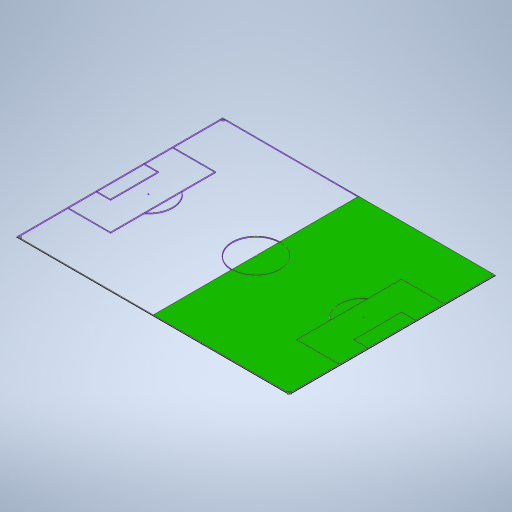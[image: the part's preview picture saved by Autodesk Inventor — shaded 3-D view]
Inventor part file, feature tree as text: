
AUTODESK INVENTOR PART (.ipt)
format: ipt  version: 2024.1 (Build 281209000, 209)  size: 520,704 bytes
history: native  units: in
note: dims shown in document units (in); Inventor stores cm internally (conversion verified against a paired STEP export)
features: extrude x42, sketch x1
ambient origin geometry x8: Origin, YZ Plane, XZ Plane, XY Plane, X Axis, Y Axis, Z Axis, Center Point
bodies: Solid3 (feature_tree), Solid4 (feature_tree), Solid5 (feature_tree), Solid6 (feature_tree), Solid7 (feature_tree), Solid8 (feature_tree), Solid9 (feature_tree), Solid10 (feature_tree), Solid11 (feature_tree)
feature tree (43):
  sketch  "Sketch2"  dims[d126=10.0in d127=0.0in d128=10.0in d129=0.0in d130=10.0in d131=0.0in d132=10.0in d133=0.0in d134=10.0in d135=0.0in d136=10.0in d137=0.0in d138=10.0in d139=0.0in d140=10.0in d141=0.0in d142=10.0in d143=0.0in d144=10.0in d145=0.0in d146=10.0in d147=0.0in d148=10.0in d149=0.0in d150=10.0in d151=0.0in d152=10.0in d153=0.0in d154=10.0in d155=0.0in d156=10.0in d157=0.0in d158=10.0in d159=0.0in d160=10.0in d161=0.0in d162=10.0in d163=0.0in d164=10.0in d165=0.0in d166=10.0in d167=0.0in d168=10.0in d169=0.0in d170=10.0in d171=0.0in d172=10.0in d173=0.0in d174=10.0in d175=0.0in d176=10.0in d177=0.0in d178=10.0in d179=0.0in d180=10.0in d181=0.0in d182=10.0in d183=0.0in d184=10.0in d185=0.0in d186=10.0in d187=0.0in d188=10.0in d189=0.0in d190=10.0in d191=0.0in d192=10.0in d193=0.0in d194=10.0in d195=0.0in d196=10.0in d197=0.0in d198=10.0in d199=0.0in d200=10.0in d201=0.0in d202=10.0in d203=0.0in d204=10.0in d205=0.0in d206=10.0in d207=0.0in d208=10.0in d209=0.0in]
  extrude  "Extrusion26"  Depth=10.0in TaperAngle=0.0deg
  extrude  "Extrusion27"  Depth=10.0in TaperAngle=0.0deg
  extrude  "Extrusion28"  Depth=10.0in TaperAngle=0.0deg
  extrude  "Extrusion29"  Depth=10.0in TaperAngle=0.0deg
  extrude  "Extrusion30"  Depth=10.0in TaperAngle=0.0deg
  extrude  "Extrusion31"  Depth=10.0in TaperAngle=0.0deg
  extrude  "Extrusion32"  Depth=10.0in TaperAngle=0.0deg
  extrude  "Extrusion33"  Depth=10.0in TaperAngle=0.0deg
  extrude  "Extrusion34"  Depth=10.0in TaperAngle=0.0deg
  extrude  "Extrusion35"  Depth=10.0in TaperAngle=0.0deg
  extrude  "Extrusion36"  Depth=10.0in TaperAngle=0.0deg
  extrude  "Extrusion37"  Depth=10.0in TaperAngle=0.0deg
  extrude  "Extrusion38"  Depth=10.0in TaperAngle=0.0deg
  extrude  "Extrusion39"  Depth=10.0in TaperAngle=0.0deg
  extrude  "Extrusion40"  Depth=10.0in TaperAngle=0.0deg
  extrude  "Extrusion41"  Depth=10.0in TaperAngle=0.0deg
  extrude  "Extrusion42"  Depth=10.0in TaperAngle=0.0deg
  extrude  "Extrusion43"  Depth=10.0in TaperAngle=0.0deg
  extrude  "Extrusion44"  Depth=10.0in TaperAngle=0.0deg
  extrude  "Extrusion45"  Depth=10.0in TaperAngle=0.0deg
  extrude  "Extrusion46"  Depth=10.0in TaperAngle=0.0deg
  extrude  "Extrusion47"  Depth=10.0in TaperAngle=0.0deg
  extrude  "Extrusion48"  Depth=10.0in TaperAngle=0.0deg
  extrude  "Extrusion49"  Depth=10.0in TaperAngle=0.0deg
  extrude  "Extrusion50"  Depth=10.0in TaperAngle=0.0deg
  extrude  "Extrusion51"  Depth=10.0in TaperAngle=0.0deg
  extrude  "Extrusion52"  Depth=10.0in TaperAngle=0.0deg
  extrude  "Extrusion53"  Depth=10.0in TaperAngle=0.0deg
  extrude  "Extrusion54"  Depth=10.0in TaperAngle=0.0deg
  extrude  "Extrusion55"  Depth=10.0in TaperAngle=0.0deg
  extrude  "Extrusion56"  Depth=10.0in TaperAngle=0.0deg
  extrude  "Extrusion57"  Depth=10.0in TaperAngle=0.0deg
  extrude  "Extrusion58"  Depth=10.0in TaperAngle=0.0deg
  extrude  "Extrusion59"  Depth=10.0in TaperAngle=0.0deg
  extrude  "Extrusion60"  Depth=10.0in TaperAngle=0.0deg
  extrude  "Extrusion61"  Depth=10.0in TaperAngle=0.0deg
  extrude  "Extrusion62"  Depth=10.0in TaperAngle=0.0deg
  extrude  "Extrusion63"  Depth=10.0in TaperAngle=0.0deg
  extrude  "Extrusion64"  Depth=10.0in TaperAngle=0.0deg
  extrude  "Extrusion65"  Depth=10.0in TaperAngle=0.0deg
  extrude  "Extrusion66"  Depth=10.0in TaperAngle=0.0deg
  extrude  "Extrusion67"  [1 undecoded]
note: 1 required parameter value undecoded (feature->parameter linkage not recoverable at this tier; creation-order binding heuristic only, values carry confidence <= 0.55)
